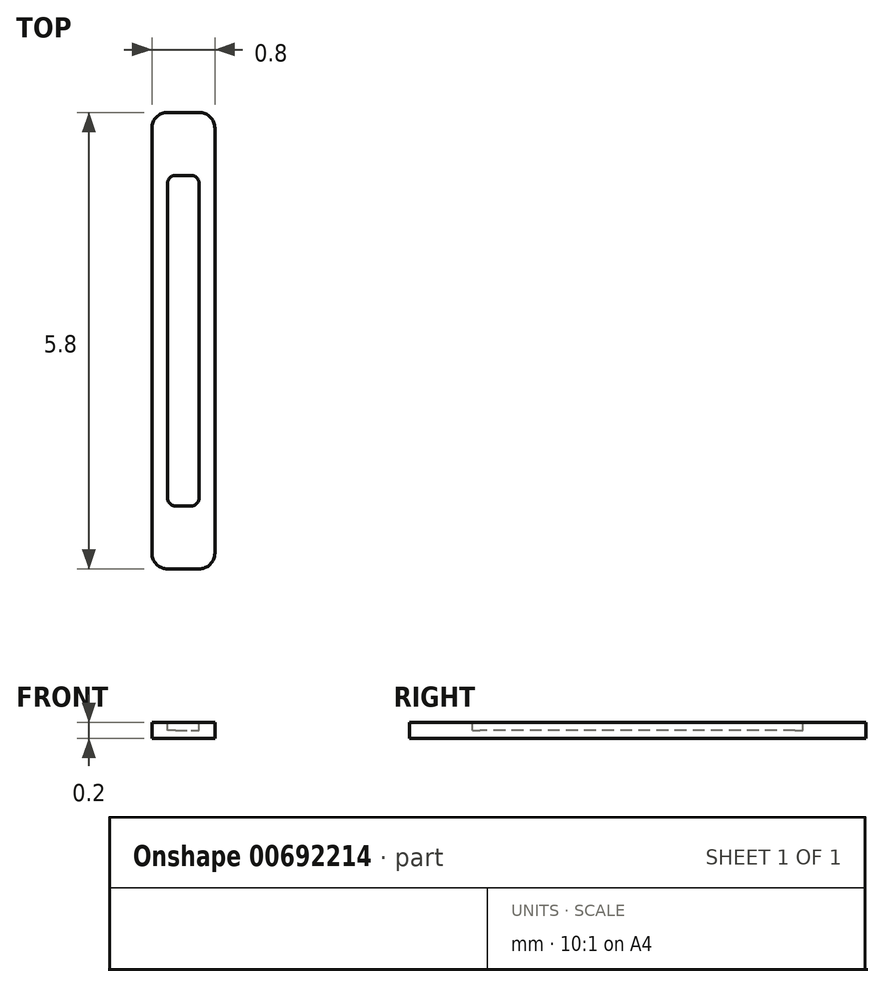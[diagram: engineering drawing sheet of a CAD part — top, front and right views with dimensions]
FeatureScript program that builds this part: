
annotation { "Feature Type Name" : "Feature", "Feature Type Description" : "" }
export const myFeature = defineFeature(function(context is Context, id is Id, definition is map)
    precondition{}
    {
        {
            var Q0;
            Q0=qCreatedBy(makeId("Top.planeOp"),FACE);
            var sketch = newSketch(context, id + "F0", { "sketchPlane" : qUnion([Q0])});
            skLineSegment(sketch, "E0.bottom", {"start": v(-0.4, 2.9) * mm, "end": v(0.4, 2.9) * mm});
            skLineSegment(sketch, "E0.top", {"start": v(-0.4, -2.9) * mm, "end": v(0.4, -2.9) * mm});
            skLineSegment(sketch, "E0.left", {"start": v(-0.4, 2.9) * mm, "end": v(-0.4, -2.9) * mm});
            skLineSegment(sketch, "E0.right", {"start": v(0.4, 2.9) * mm, "end": v(0.4, -2.9) * mm});
            skSolve(sketch);
        }
        {
            var Q0;
            Q0=makeQuery(id+"F0.imprint","IMPRINT",FACE,{"disambiguationData":[TD([[makeQuery(id+"F0.imprint","IMPRINT",EDGE,{"derivedFrom":sQuery(id+"F0.wireOp",EDGE,"E0.bottom")}),-1.0]])]});
            extrude(context, id + "F1", {"entities" : qUnion([Q0]), "depth" : 0.2 * mm, "offsetDistance" : 25 * mm});
        }
        {
            var Q0;
            Q0=makeQuery(id+"F1.opExtrude","CAP_FACE",FACE,{"disambiguationData":[OSD([sQuery(id+"F0.wireOp",EDGE,"E0.bottom"),sQuery(id+"F0.wireOp",EDGE,"E0.top"),sQuery(id+"F0.wireOp",EDGE,"E0.left"),sQuery(id+"F0.wireOp",EDGE,"E0.right")])],"isStart":false});
            var sketch = newSketch(context, id + "F2", { "sketchPlane" : qUnion([Q0])});
            skLineSegment(sketch, "E1", {"start": v(0, 2.1) * mm, "end": v(-0.2, 2.1) * mm});
            skLineSegment(sketch, "E2", {"start": v(-0.2, 2.1) * mm, "end": v(-0.2, -2.1) * mm});
            skLineSegment(sketch, "E3.MirrorCS", {"start": v(0, -2.1) * mm, "end": v(-0.2, -2.1) * mm});
            skLineSegment(sketch, "E4.MirrorCS", {"start": v(0, 2.1) * mm, "end": v(0.2, 2.1) * mm});
            skLineSegment(sketch, "E5.MirrorCS", {"start": v(0.2, 2.1) * mm, "end": v(0.2, -2.1) * mm});
            skLineSegment(sketch, "E6.MirrorCS", {"start": v(0, -2.1) * mm, "end": v(0.2, -2.1) * mm});
            skSolve(sketch);
        }
        {
            var Q0;
            Q0 = qSketchRegion(id + "F2", true);
            extrude(context, id + "F3", {"entities" : qUnion([Q0]), "operationType" : NewBodyOperationType.REMOVE, "oppositeDirection" : true, "depth" : 0.1 * mm, "offsetDistance" : 25 * mm});
        }
        {
            var Q0;
            Q0=makeQuery(id+"F1.opExtrude","SWEPT_EDGE",EDGE,{"disambiguationData":[OSD([sQuery(id+"F0.wireOp",EDGE,"E0.bottom"),sQuery(id+"F0.wireOp",EDGE,"E0.right")])]});
            var Q1;
            Q1=makeQuery(id+"F1.opExtrude","SWEPT_EDGE",EDGE,{"disambiguationData":[OSD([sQuery(id+"F0.wireOp",EDGE,"E0.bottom"),sQuery(id+"F0.wireOp",EDGE,"E0.left")])]});
            var Q2;
            Q2=makeQuery(id+"F1.opExtrude","SWEPT_EDGE",EDGE,{"disambiguationData":[OSD([sQuery(id+"F0.wireOp",EDGE,"E0.top"),sQuery(id+"F0.wireOp",EDGE,"E0.right")])]});
            var Q3;
            Q3=makeQuery(id+"F1.opExtrude","SWEPT_EDGE",EDGE,{"disambiguationData":[OSD([sQuery(id+"F0.wireOp",EDGE,"E0.top"),sQuery(id+"F0.wireOp",EDGE,"E0.left")])]});
            fillet(context, id + "F4", {"entities" : qUnion([Q0, Q1, Q2, Q3]), "radius" : 0.2 * mm, "tangentPropagation" : true, "allowEdgeOverflow" : false});
        }
        {
            var Q0;
            Q0=makeQuery(id+"F3.boolean.opBoolean","COPY",EDGE,{"derivedFrom":makeQuery(id+"F3.opExtrude","SWEPT_EDGE",EDGE,{"disambiguationData":[OSD([sQuery(id+"F2.wireOp",EDGE,"E4.MirrorCS"),sQuery(id+"F2.wireOp",EDGE,"E5.MirrorCS")])]})});
            var Q1;
            Q1=makeQuery(id+"F3.boolean.opBoolean","COPY",EDGE,{"derivedFrom":makeQuery(id+"F3.opExtrude","SWEPT_EDGE",EDGE,{"disambiguationData":[OSD([sQuery(id+"F2.wireOp",EDGE,"E1"),sQuery(id+"F2.wireOp",EDGE,"E2")])]})});
            var Q2;
            Q2=makeQuery(id+"F3.boolean.opBoolean","COPY",EDGE,{"derivedFrom":makeQuery(id+"F3.opExtrude","SWEPT_EDGE",EDGE,{"disambiguationData":[OSD([sQuery(id+"F2.wireOp",EDGE,"E2"),sQuery(id+"F2.wireOp",EDGE,"E3.MirrorCS")])]})});
            var Q3;
            Q3=makeQuery(id+"F3.boolean.opBoolean","COPY",EDGE,{"derivedFrom":makeQuery(id+"F3.opExtrude","SWEPT_EDGE",EDGE,{"disambiguationData":[OSD([sQuery(id+"F2.wireOp",EDGE,"E5.MirrorCS"),sQuery(id+"F2.wireOp",EDGE,"E6.MirrorCS")])]})});
            fillet(context, id + "F5", {"entities" : qUnion([Q0, Q1, Q2, Q3]), "radius" : 0.1 * mm, "tangentPropagation" : true, "allowEdgeOverflow" : false});
        }
    });
